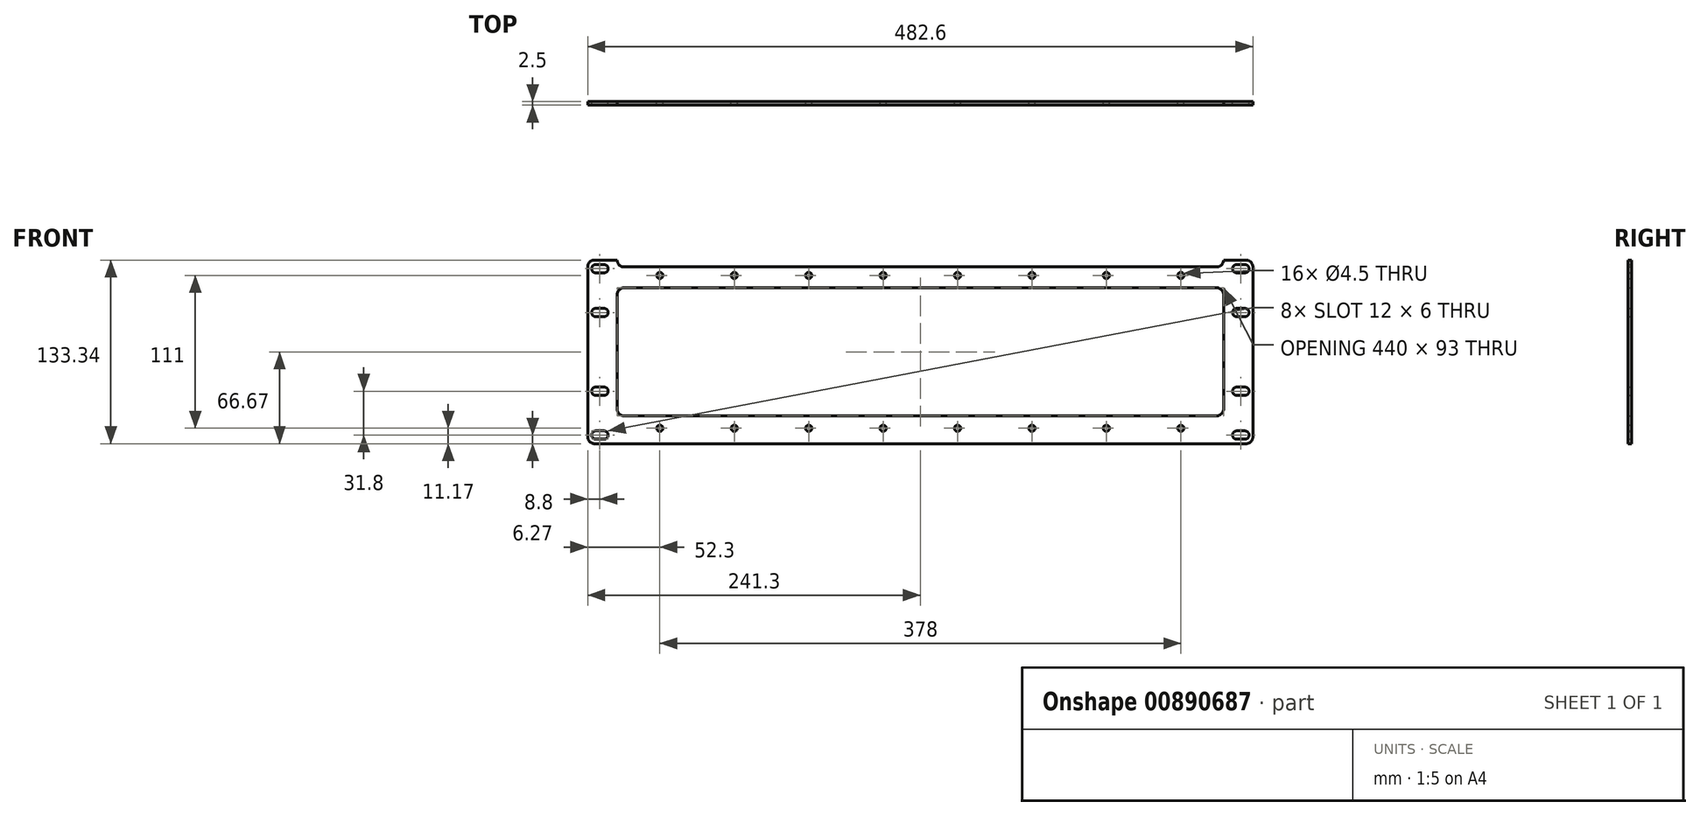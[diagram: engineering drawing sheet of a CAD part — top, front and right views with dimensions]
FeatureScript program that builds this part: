
annotation { "Feature Type Name" : "Feature", "Feature Type Description" : "" }
export const myFeature = defineFeature(function(context is Context, id is Id, definition is map)
    precondition{}
    {
        {
            var Q0;
            Q0=qCreatedBy(makeId("Front.planeOp"),FACE);
            var sketch = newSketch(context, id + "F0", { "sketchPlane" : qUnion([Q0])});
            skLineSegment(sketch, "E0.bottom", {"start": v(236.3, 66.67) * mm, "end": v(-236.3, 66.67) * mm});
            skLineSegment(sketch, "E0.top", {"start": v(236.3, -66.67) * mm, "end": v(-236.3, -66.67) * mm});
            skLineSegment(sketch, "E0.left", {"start": v(241.3, 61.67) * mm, "end": v(241.3, -61.67) * mm});
            skLineSegment(sketch, "E0.right", {"start": v(-241.3, 61.67) * mm, "end": v(-241.3, -61.67) * mm});
            skPoint(sketch, "E0.middle", {"position": v(0, 0) * mm});
            skLineSegment(sketch, "E1.bottom", {"start": v(232.5, 60.4) * mm, "end": v(-232.5, 60.4) * mm, "construction": true});
            skLineSegment(sketch, "E1.top", {"start": v(232.5, -60.4) * mm, "end": v(-232.5, -60.4) * mm, "construction": true});
            skLineSegment(sketch, "E1.left", {"start": v(232.5, 60.4) * mm, "end": v(232.5, -60.4) * mm, "construction": true});
            skLineSegment(sketch, "E1.right", {"start": v(-232.5, 60.4) * mm, "end": v(-232.5, -60.4) * mm, "construction": true});
            skLineSegment(sketch, "E2.bottom", {"start": v(232.5, 28.6) * mm, "end": v(-232.5, 28.6) * mm, "construction": true});
            skLineSegment(sketch, "E2.top", {"start": v(232.5, -28.6) * mm, "end": v(-232.5, -28.6) * mm, "construction": true});
            skLineSegment(sketch, "E2.left", {"start": v(232.5, 28.6) * mm, "end": v(232.5, -28.6) * mm, "construction": true});
            skLineSegment(sketch, "E2.right", {"start": v(-232.5, 28.6) * mm, "end": v(-232.5, -28.6) * mm, "construction": true});
            skPoint(sketch, "E3.middle", {"position": v(0, 66.67) * mm});
            skLineSegment(sketch, "E4", {"start": v(220, 66.68) * mm, "end": v(220, 66.68) * mm});
            skLineSegment(sketch, "E5", {"start": v(-220, 66.67) * mm, "end": v(-220, 66.67) * mm});
            skPoint(sketch, "E6.visualSharp", {"position": v(-241.3, 66.67) * mm});
            skArc(sketch, "E6.filletArc", {"start": v(-236.3, 66.67) * mm, "mid": v(-239.84, 65.21) * mm, "end": v(-241.3, 61.67) * mm});
            skPoint(sketch, "E7.visualSharp", {"position": v(-241.3, -66.67) * mm});
            skArc(sketch, "E7.filletArc", {"start": v(-241.3, -61.67) * mm, "mid": v(-239.84, -65.21) * mm, "end": v(-236.3, -66.67) * mm});
            skPoint(sketch, "E8.visualSharp", {"position": v(241.3, -66.67) * mm});
            skArc(sketch, "E8.filletArc", {"start": v(236.3, -66.67) * mm, "mid": v(239.84, -65.21) * mm, "end": v(241.3, -61.67) * mm});
            skPoint(sketch, "E9.visualSharp", {"position": v(241.3, 66.67) * mm});
            skArc(sketch, "E9.filletArc", {"start": v(241.3, 61.67) * mm, "mid": v(239.84, 65.21) * mm, "end": v(236.3, 66.67) * mm});
            skLineSegment(sketch, "E10", {"start": v(215, 61.68) * mm, "end": v(-215, 61.67) * mm});
            skPoint(sketch, "E11.visualSharp", {"position": v(-220, 61.67) * mm});
            skArc(sketch, "E11.filletArc", {"start": v(-220, 66.67) * mm, "mid": v(-218.54, 63.14) * mm, "end": v(-215, 61.67) * mm});
            skPoint(sketch, "E12.visualSharp", {"position": v(220, 61.68) * mm});
            skArc(sketch, "E12.filletArc", {"start": v(215, 61.68) * mm, "mid": v(218.54, 63.14) * mm, "end": v(220, 66.68) * mm});
            skSolve(sketch);
        }
        {
            var Q0;
            Q0=makeQuery(id+"F0.imprint","IMPRINT",FACE,{"disambiguationData":[TD([[makeQuery(id+"F0.imprint","IMPRINT",EDGE,{"derivedFrom":sQuery(id+"F0.wireOp",EDGE,"E0.bottom")}),1.0]])]});
            var sketch = newSketch(context, id + "F1", { "sketchPlane" : qUnion([Q0])});
            skPoint(sketch, "E13.0", {"position": v(-232.5, 60.4) * mm});
            skLineSegment(sketch, "E14.bottom", {"start": v(-226.5, 63.4) * mm, "end": v(-238.5, 63.4) * mm, "construction": true});
            skLineSegment(sketch, "E14.top", {"start": v(-226.5, 57.4) * mm, "end": v(-238.5, 57.4) * mm, "construction": true});
            skLineSegment(sketch, "E14.left", {"start": v(-226.5, 63.4) * mm, "end": v(-226.5, 57.4) * mm, "construction": true});
            skLineSegment(sketch, "E14.right", {"start": v(-238.5, 63.4) * mm, "end": v(-238.5, 57.4) * mm, "construction": true});
            skLineSegment(sketch, "E15.bottom", {"start": v(-229.5, 63.4) * mm, "end": v(-235.5, 63.4) * mm, "construction": true});
            skLineSegment(sketch, "E15.top", {"start": v(-229.5, 57.4) * mm, "end": v(-235.5, 57.4) * mm, "construction": true});
            skLineSegment(sketch, "E15.left", {"start": v(-229.5, 63.4) * mm, "end": v(-229.5, 57.4) * mm, "construction": true});
            skLineSegment(sketch, "E15.right", {"start": v(-235.5, 63.4) * mm, "end": v(-235.5, 57.4) * mm, "construction": true});
            skLineSegment(sketch, "E16", {"start": v(-229.5, 63.4) * mm, "end": v(-235.5, 63.4) * mm});
            skLineSegment(sketch, "E17", {"start": v(-229.5, 57.4) * mm, "end": v(-235.5, 57.4) * mm});
            skArc(sketch, "E18", {"start": v(-229.5, 63.4) * mm, "mid": v(-226.5, 60.4) * mm, "end": v(-229.5, 57.4) * mm});
            skArc(sketch, "E19", {"start": v(-235.5, 63.4) * mm, "mid": v(-238.5, 60.4) * mm, "end": v(-235.5, 57.4) * mm});
            skPoint(sketch, "E20.0", {"position": v(-232.5, 28.6) * mm});
            skLineSegment(sketch, "E21.bottom", {"start": v(-226.5, 31.6) * mm, "end": v(-238.5, 31.6) * mm, "construction": true});
            skLineSegment(sketch, "E21.top", {"start": v(-226.5, 25.6) * mm, "end": v(-238.5, 25.6) * mm, "construction": true});
            skLineSegment(sketch, "E21.left", {"start": v(-226.5, 31.6) * mm, "end": v(-226.5, 25.6) * mm, "construction": true});
            skLineSegment(sketch, "E21.right", {"start": v(-238.5, 31.6) * mm, "end": v(-238.5, 25.6) * mm, "construction": true});
            skLineSegment(sketch, "E22.bottom", {"start": v(-229.5, 31.6) * mm, "end": v(-235.5, 31.6) * mm, "construction": true});
            skLineSegment(sketch, "E22.top", {"start": v(-229.5, 25.6) * mm, "end": v(-235.5, 25.6) * mm, "construction": true});
            skLineSegment(sketch, "E22.left", {"start": v(-229.5, 31.6) * mm, "end": v(-229.5, 25.6) * mm, "construction": true});
            skLineSegment(sketch, "E22.right", {"start": v(-235.5, 31.6) * mm, "end": v(-235.5, 25.6) * mm, "construction": true});
            skLineSegment(sketch, "E23", {"start": v(-229.5, 31.6) * mm, "end": v(-235.5, 31.6) * mm});
            skLineSegment(sketch, "E24", {"start": v(-229.5, 25.6) * mm, "end": v(-235.5, 25.6) * mm});
            skArc(sketch, "E25", {"start": v(-229.5, 31.6) * mm, "mid": v(-226.5, 28.6) * mm, "end": v(-229.5, 25.6) * mm});
            skArc(sketch, "E26", {"start": v(-235.5, 31.6) * mm, "mid": v(-238.5, 28.6) * mm, "end": v(-235.5, 25.6) * mm});
            skPoint(sketch, "E27.0", {"position": v(-232.5, -28.6) * mm});
            skPoint(sketch, "E28.0", {"position": v(-232.5, -60.4) * mm});
            skLineSegment(sketch, "E29.bottom", {"start": v(-226.5, -25.6) * mm, "end": v(-238.5, -25.6) * mm, "construction": true});
            skLineSegment(sketch, "E29.top", {"start": v(-226.5, -31.6) * mm, "end": v(-238.5, -31.6) * mm, "construction": true});
            skLineSegment(sketch, "E29.left", {"start": v(-226.5, -25.6) * mm, "end": v(-226.5, -31.6) * mm, "construction": true});
            skLineSegment(sketch, "E29.right", {"start": v(-238.5, -25.6) * mm, "end": v(-238.5, -31.6) * mm, "construction": true});
            skLineSegment(sketch, "E30.bottom", {"start": v(-229.5, -25.6) * mm, "end": v(-235.5, -25.6) * mm, "construction": true});
            skLineSegment(sketch, "E30.top", {"start": v(-229.5, -31.6) * mm, "end": v(-235.5, -31.6) * mm, "construction": true});
            skLineSegment(sketch, "E30.left", {"start": v(-229.5, -25.6) * mm, "end": v(-229.5, -31.6) * mm, "construction": true});
            skLineSegment(sketch, "E30.right", {"start": v(-235.5, -25.6) * mm, "end": v(-235.5, -31.6) * mm, "construction": true});
            skLineSegment(sketch, "E31", {"start": v(-229.5, -25.6) * mm, "end": v(-235.5, -25.6) * mm});
            skLineSegment(sketch, "E32", {"start": v(-229.5, -31.6) * mm, "end": v(-235.5, -31.6) * mm});
            skArc(sketch, "E33", {"start": v(-229.5, -25.6) * mm, "mid": v(-226.5, -28.6) * mm, "end": v(-229.5, -31.6) * mm});
            skArc(sketch, "E34", {"start": v(-235.5, -25.6) * mm, "mid": v(-238.5, -28.6) * mm, "end": v(-235.5, -31.6) * mm});
            skLineSegment(sketch, "E35.bottom", {"start": v(-226.5, -57.4) * mm, "end": v(-238.5, -57.4) * mm, "construction": true});
            skLineSegment(sketch, "E35.top", {"start": v(-226.5, -63.4) * mm, "end": v(-238.5, -63.4) * mm, "construction": true});
            skLineSegment(sketch, "E35.left", {"start": v(-226.5, -57.4) * mm, "end": v(-226.5, -63.4) * mm, "construction": true});
            skLineSegment(sketch, "E35.right", {"start": v(-238.5, -57.4) * mm, "end": v(-238.5, -63.4) * mm, "construction": true});
            skLineSegment(sketch, "E36.bottom", {"start": v(-229.5, -57.4) * mm, "end": v(-235.5, -57.4) * mm, "construction": true});
            skLineSegment(sketch, "E36.top", {"start": v(-229.5, -63.4) * mm, "end": v(-235.5, -63.4) * mm, "construction": true});
            skLineSegment(sketch, "E36.left", {"start": v(-229.5, -57.4) * mm, "end": v(-229.5, -63.4) * mm, "construction": true});
            skLineSegment(sketch, "E36.right", {"start": v(-235.5, -57.4) * mm, "end": v(-235.5, -63.4) * mm, "construction": true});
            skLineSegment(sketch, "E37", {"start": v(-229.5, -57.4) * mm, "end": v(-235.5, -57.4) * mm});
            skLineSegment(sketch, "E38", {"start": v(-229.5, -63.4) * mm, "end": v(-235.5, -63.4) * mm});
            skArc(sketch, "E39", {"start": v(-229.5, -57.4) * mm, "mid": v(-226.5, -60.4) * mm, "end": v(-229.5, -63.4) * mm});
            skArc(sketch, "E40", {"start": v(-235.5, -57.4) * mm, "mid": v(-238.5, -60.4) * mm, "end": v(-235.5, -63.4) * mm});
            skPoint(sketch, "E41.0", {"position": v(232.5, 60.4) * mm});
            skPoint(sketch, "E42.0", {"position": v(232.5, 28.6) * mm});
            skPoint(sketch, "E43.0", {"position": v(232.5, -28.6) * mm});
            skPoint(sketch, "E44.0", {"position": v(232.5, -60.4) * mm});
            skLineSegment(sketch, "E45.bottom", {"start": v(238.5, 63.4) * mm, "end": v(226.5, 63.4) * mm, "construction": true});
            skLineSegment(sketch, "E45.top", {"start": v(238.5, 57.4) * mm, "end": v(226.5, 57.4) * mm, "construction": true});
            skLineSegment(sketch, "E45.left", {"start": v(238.5, 63.4) * mm, "end": v(238.5, 57.4) * mm, "construction": true});
            skLineSegment(sketch, "E45.right", {"start": v(226.5, 63.4) * mm, "end": v(226.5, 57.4) * mm, "construction": true});
            skLineSegment(sketch, "E46.bottom", {"start": v(235.5, 63.4) * mm, "end": v(229.5, 63.4) * mm, "construction": true});
            skLineSegment(sketch, "E46.top", {"start": v(235.5, 57.4) * mm, "end": v(229.5, 57.4) * mm, "construction": true});
            skLineSegment(sketch, "E46.left", {"start": v(235.5, 63.4) * mm, "end": v(235.5, 57.4) * mm, "construction": true});
            skLineSegment(sketch, "E46.right", {"start": v(229.5, 63.4) * mm, "end": v(229.5, 57.4) * mm, "construction": true});
            skLineSegment(sketch, "E47", {"start": v(235.5, 63.4) * mm, "end": v(229.5, 63.4) * mm});
            skLineSegment(sketch, "E48", {"start": v(235.5, 57.4) * mm, "end": v(229.5, 57.4) * mm});
            skArc(sketch, "E49", {"start": v(235.5, 63.4) * mm, "mid": v(238.5, 60.4) * mm, "end": v(235.5, 57.4) * mm});
            skArc(sketch, "E50", {"start": v(229.5, 63.4) * mm, "mid": v(226.5, 60.4) * mm, "end": v(229.5, 57.4) * mm});
            skLineSegment(sketch, "E51.bottom", {"start": v(238.5, 31.6) * mm, "end": v(226.5, 31.6) * mm, "construction": true});
            skLineSegment(sketch, "E51.top", {"start": v(238.5, 25.6) * mm, "end": v(226.5, 25.6) * mm, "construction": true});
            skLineSegment(sketch, "E51.left", {"start": v(238.5, 31.6) * mm, "end": v(238.5, 25.6) * mm, "construction": true});
            skLineSegment(sketch, "E51.right", {"start": v(226.5, 31.6) * mm, "end": v(226.5, 25.6) * mm, "construction": true});
            skLineSegment(sketch, "E52.bottom", {"start": v(235.5, 31.6) * mm, "end": v(229.5, 31.6) * mm, "construction": true});
            skLineSegment(sketch, "E52.top", {"start": v(235.5, 25.6) * mm, "end": v(229.5, 25.6) * mm, "construction": true});
            skLineSegment(sketch, "E52.left", {"start": v(235.5, 31.6) * mm, "end": v(235.5, 25.6) * mm, "construction": true});
            skLineSegment(sketch, "E52.right", {"start": v(229.5, 31.6) * mm, "end": v(229.5, 25.6) * mm, "construction": true});
            skLineSegment(sketch, "E53", {"start": v(235.5, 31.6) * mm, "end": v(229.5, 31.6) * mm});
            skLineSegment(sketch, "E54", {"start": v(235.5, 25.6) * mm, "end": v(229.5, 25.6) * mm});
            skArc(sketch, "E55", {"start": v(235.5, 31.6) * mm, "mid": v(238.5, 28.6) * mm, "end": v(235.5, 25.6) * mm});
            skArc(sketch, "E56", {"start": v(229.5, 31.6) * mm, "mid": v(226.5, 28.6) * mm, "end": v(229.5, 25.6) * mm});
            skLineSegment(sketch, "E57.bottom", {"start": v(238.5, -25.6) * mm, "end": v(226.5, -25.6) * mm, "construction": true});
            skLineSegment(sketch, "E57.top", {"start": v(238.5, -31.6) * mm, "end": v(226.5, -31.6) * mm, "construction": true});
            skLineSegment(sketch, "E57.left", {"start": v(238.5, -25.6) * mm, "end": v(238.5, -31.6) * mm, "construction": true});
            skLineSegment(sketch, "E57.right", {"start": v(226.5, -25.6) * mm, "end": v(226.5, -31.6) * mm, "construction": true});
            skLineSegment(sketch, "E58.bottom", {"start": v(235.5, -25.6) * mm, "end": v(229.5, -25.6) * mm, "construction": true});
            skLineSegment(sketch, "E58.top", {"start": v(235.5, -31.6) * mm, "end": v(229.5, -31.6) * mm, "construction": true});
            skLineSegment(sketch, "E58.left", {"start": v(235.5, -25.6) * mm, "end": v(235.5, -31.6) * mm, "construction": true});
            skLineSegment(sketch, "E58.right", {"start": v(229.5, -25.6) * mm, "end": v(229.5, -31.6) * mm, "construction": true});
            skLineSegment(sketch, "E59", {"start": v(235.5, -25.6) * mm, "end": v(229.5, -25.6) * mm});
            skLineSegment(sketch, "E60", {"start": v(235.5, -31.6) * mm, "end": v(229.5, -31.6) * mm});
            skArc(sketch, "E61", {"start": v(235.5, -25.6) * mm, "mid": v(238.5, -28.6) * mm, "end": v(235.5, -31.6) * mm});
            skArc(sketch, "E62", {"start": v(229.5, -25.6) * mm, "mid": v(226.5, -28.6) * mm, "end": v(229.5, -31.6) * mm});
            skLineSegment(sketch, "E63.bottom", {"start": v(238.5, -57.4) * mm, "end": v(226.5, -57.4) * mm, "construction": true});
            skLineSegment(sketch, "E63.top", {"start": v(238.5, -63.4) * mm, "end": v(226.5, -63.4) * mm, "construction": true});
            skLineSegment(sketch, "E63.left", {"start": v(238.5, -57.4) * mm, "end": v(238.5, -63.4) * mm, "construction": true});
            skLineSegment(sketch, "E63.right", {"start": v(226.5, -57.4) * mm, "end": v(226.5, -63.4) * mm, "construction": true});
            skLineSegment(sketch, "E64.bottom", {"start": v(235.5, -57.4) * mm, "end": v(229.5, -57.4) * mm, "construction": true});
            skLineSegment(sketch, "E64.top", {"start": v(235.5, -63.4) * mm, "end": v(229.5, -63.4) * mm, "construction": true});
            skLineSegment(sketch, "E64.left", {"start": v(235.5, -57.4) * mm, "end": v(235.5, -63.4) * mm, "construction": true});
            skLineSegment(sketch, "E64.right", {"start": v(229.5, -57.4) * mm, "end": v(229.5, -63.4) * mm, "construction": true});
            skLineSegment(sketch, "E65", {"start": v(235.5, -57.4) * mm, "end": v(229.5, -57.4) * mm});
            skLineSegment(sketch, "E66", {"start": v(235.5, -63.4) * mm, "end": v(229.5, -63.4) * mm});
            skArc(sketch, "E67", {"start": v(235.5, -57.4) * mm, "mid": v(238.5, -60.4) * mm, "end": v(235.5, -63.4) * mm});
            skArc(sketch, "E68", {"start": v(229.5, -57.4) * mm, "mid": v(226.5, -60.4) * mm, "end": v(229.5, -63.4) * mm});
            skLineSegment(sketch, "E69.bottom", {"start": v(215, 46.5) * mm, "end": v(-215, 46.5) * mm});
            skLineSegment(sketch, "E69.top", {"start": v(215, -46.5) * mm, "end": v(-215, -46.5) * mm});
            skLineSegment(sketch, "E69.left", {"start": v(220, 41.5) * mm, "end": v(220, -41.5) * mm});
            skLineSegment(sketch, "E69.right", {"start": v(-220, 41.5) * mm, "end": v(-220, -41.5) * mm});
            skPoint(sketch, "E69.middle", {"position": v(0, 0) * mm});
            skPoint(sketch, "E70.visualSharp", {"position": v(-220, 46.5) * mm});
            skArc(sketch, "E70.filletArc", {"start": v(-215, 46.5) * mm, "mid": v(-218.54, 45.04) * mm, "end": v(-220, 41.5) * mm});
            skPoint(sketch, "E71.visualSharp", {"position": v(-220, -46.5) * mm});
            skArc(sketch, "E71.filletArc", {"start": v(-220, -41.5) * mm, "mid": v(-218.54, -45.04) * mm, "end": v(-215, -46.5) * mm});
            skPoint(sketch, "E72.visualSharp", {"position": v(220, -46.5) * mm});
            skArc(sketch, "E72.filletArc", {"start": v(215, -46.5) * mm, "mid": v(218.54, -45.04) * mm, "end": v(220, -41.5) * mm});
            skPoint(sketch, "E73.visualSharp", {"position": v(220, 46.5) * mm});
            skArc(sketch, "E73.filletArc", {"start": v(220, 41.5) * mm, "mid": v(218.54, 45.04) * mm, "end": v(215, 46.5) * mm});
            skLineSegment(sketch, "E74", {"start": v(-220.15, -55.5) * mm, "end": v(219.85, -55.5) * mm, "construction": true});
            skLineSegment(sketch, "E75", {"start": v(0, -55.5) * mm, "end": v(27, -55.5) * mm, "construction": true});
            skLineSegment(sketch, "E76", {"start": v(27, -55.5) * mm, "end": v(81, -55.5) * mm, "construction": true});
            skLineSegment(sketch, "E77", {"start": v(81, -55.5) * mm, "end": v(135, -55.5) * mm, "construction": true});
            skLineSegment(sketch, "E78", {"start": v(135, -55.5) * mm, "end": v(189, -55.5) * mm, "construction": true});
            skCircle(sketch, "E79", {"center": v(27, -55.5) * mm, "radius": 2.25 * mm});
            skCircle(sketch, "E80", {"center": v(81, -55.5) * mm, "radius": 2.25 * mm});
            skCircle(sketch, "E81", {"center": v(135, -55.5) * mm, "radius": 2.25 * mm});
            skCircle(sketch, "E82", {"center": v(189, -55.5) * mm, "radius": 2.25 * mm});
            skCircle(sketch, "E83.MirrorC", {"center": v(-27, -55.5) * mm, "radius": 2.25 * mm});
            skCircle(sketch, "E84.MirrorC", {"center": v(-81, -55.5) * mm, "radius": 2.25 * mm});
            skCircle(sketch, "E85.MirrorC", {"center": v(-135, -55.5) * mm, "radius": 2.25 * mm});
            skCircle(sketch, "E86.MirrorC", {"center": v(-189, -55.5) * mm, "radius": 2.25 * mm});
            skCircle(sketch, "E87.MirrorC", {"center": v(-189, 55.5) * mm, "radius": 2.25 * mm});
            skCircle(sketch, "E88.MirrorC", {"center": v(-135, 55.5) * mm, "radius": 2.25 * mm});
            skCircle(sketch, "E89.MirrorC", {"center": v(-81, 55.5) * mm, "radius": 2.25 * mm});
            skCircle(sketch, "E90.MirrorC", {"center": v(-27, 55.5) * mm, "radius": 2.25 * mm});
            skCircle(sketch, "E91.MirrorC", {"center": v(27, 55.5) * mm, "radius": 2.25 * mm});
            skCircle(sketch, "E92.MirrorC", {"center": v(81, 55.5) * mm, "radius": 2.25 * mm});
            skCircle(sketch, "E93.MirrorC", {"center": v(135, 55.5) * mm, "radius": 2.25 * mm});
            skCircle(sketch, "E94.MirrorC", {"center": v(189, 55.5) * mm, "radius": 2.25 * mm});
            skSolve(sketch);
        }
        {
            var Q0;
            Q0=makeQuery(id+"F1.imprint","IMPRINT",FACE,{"disambiguationData":[TD([[makeQuery(id+"F1.imprint","IMPRINT",EDGE,{"derivedFrom":sQuery(id+"F1.wireOp",EDGE,"E16")}),-1.0]])]});
            extrude(context, id + "F2", {"entities" : qUnion([Q0]), "depth" : 2.5 * mm, "offsetDistance" : 25 * mm});
        }
    });
